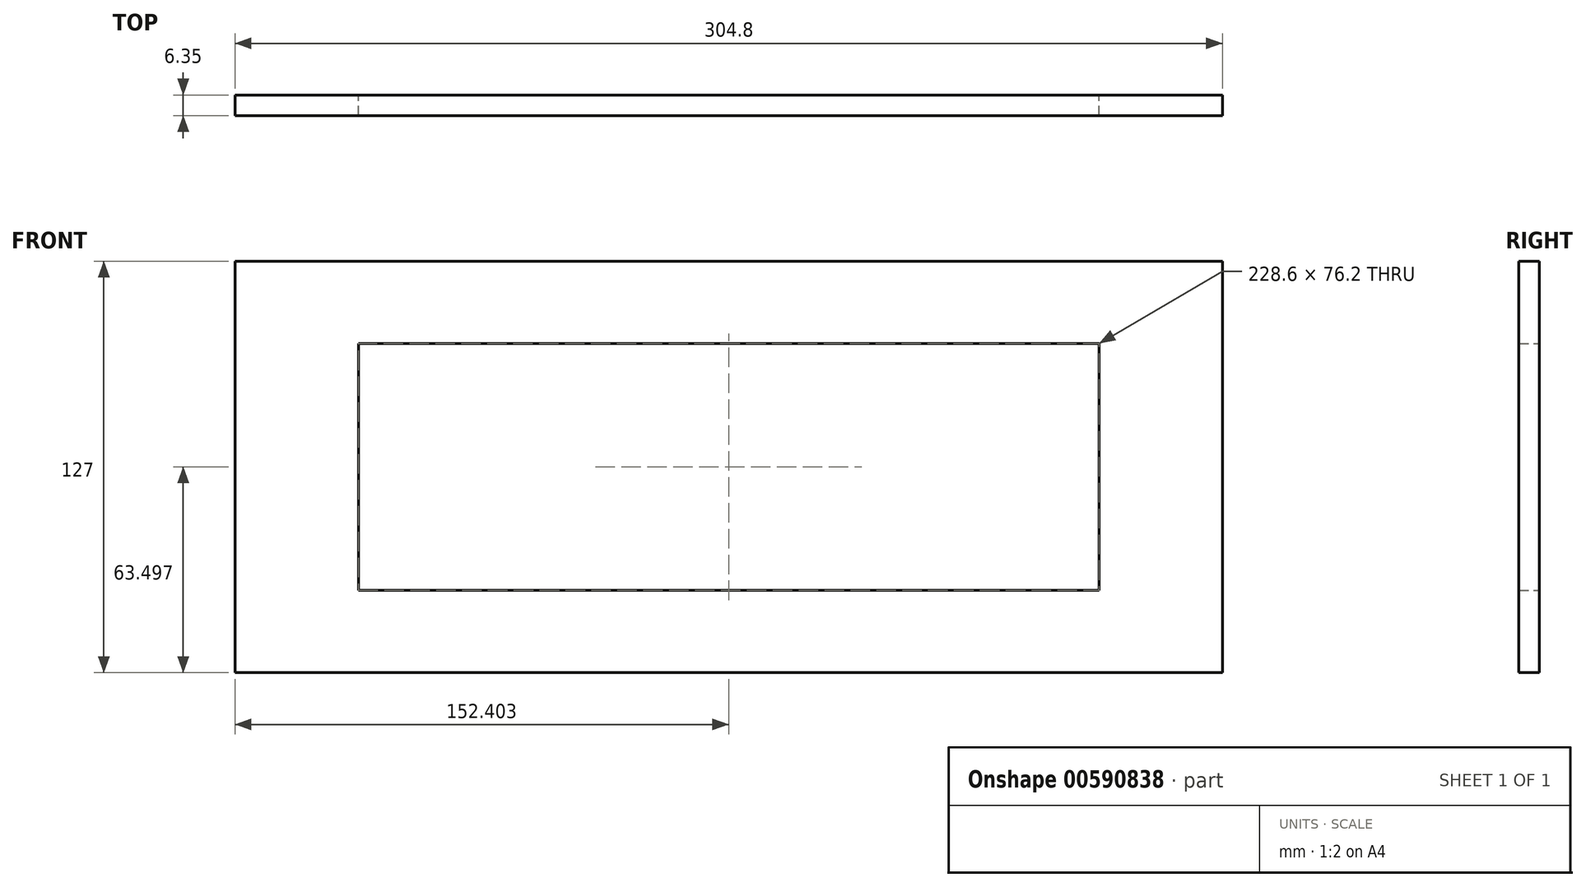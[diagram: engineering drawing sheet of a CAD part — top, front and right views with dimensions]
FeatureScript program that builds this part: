
annotation { "Feature Type Name" : "Feature", "Feature Type Description" : "" }
export const myFeature = defineFeature(function(context is Context, id is Id, definition is map)
    precondition{}
    {
        {
            var Q0;
            Q0=qCreatedBy(makeId("Front.planeOp"),FACE);
            var sketch = newSketch(context, id + "F0", { "sketchPlane" : qUnion([Q0])});
            skLineSegment(sketch, "E0", {"start": v(-186.9, 138.4) * mm, "end": v(-165.33, 138.4) * mm});
            skLineSegment(sketch, "E1", {"start": v(-165.33, -39.61) * mm, "end": v(139.47, -39.61) * mm});
            skLineSegment(sketch, "E2", {"start": v(139.47, -39.61) * mm, "end": v(139.47, -166.61) * mm});
            skLineSegment(sketch, "E3", {"start": v(139.47, -166.61) * mm, "end": v(-165.33, -166.61) * mm});
            skLineSegment(sketch, "E4", {"start": v(-165.33, -166.61) * mm, "end": v(-165.33, -39.61) * mm});
            skLineSegment(sketch, "E5.bottom", {"start": v(-127.23, -65.01) * mm, "end": v(101.37, -65.01) * mm});
            skLineSegment(sketch, "E5.top", {"start": v(-127.23, -141.21) * mm, "end": v(101.37, -141.21) * mm});
            skLineSegment(sketch, "E5.left", {"start": v(-127.23, -65.01) * mm, "end": v(-127.23, -141.21) * mm});
            skLineSegment(sketch, "E5.right", {"start": v(101.37, -65.01) * mm, "end": v(101.37, -141.21) * mm});
            skSolve(sketch);
        }
        {
            var Q0;
            Q0=makeQuery(id+"F0.imprint","IMPRINT",FACE,{"disambiguationData":[TD([[makeQuery(id+"F0.imprint","IMPRINT",EDGE,{"derivedFrom":sQuery(id+"F0.wireOp",EDGE,"E1")}),-1.0]])]});
            extrude(context, id + "F1", {"entities" : qUnion([Q0]), "depth" : 6.35 * mm, "offsetDistance" : 25.4 * mm});
        }
    });
